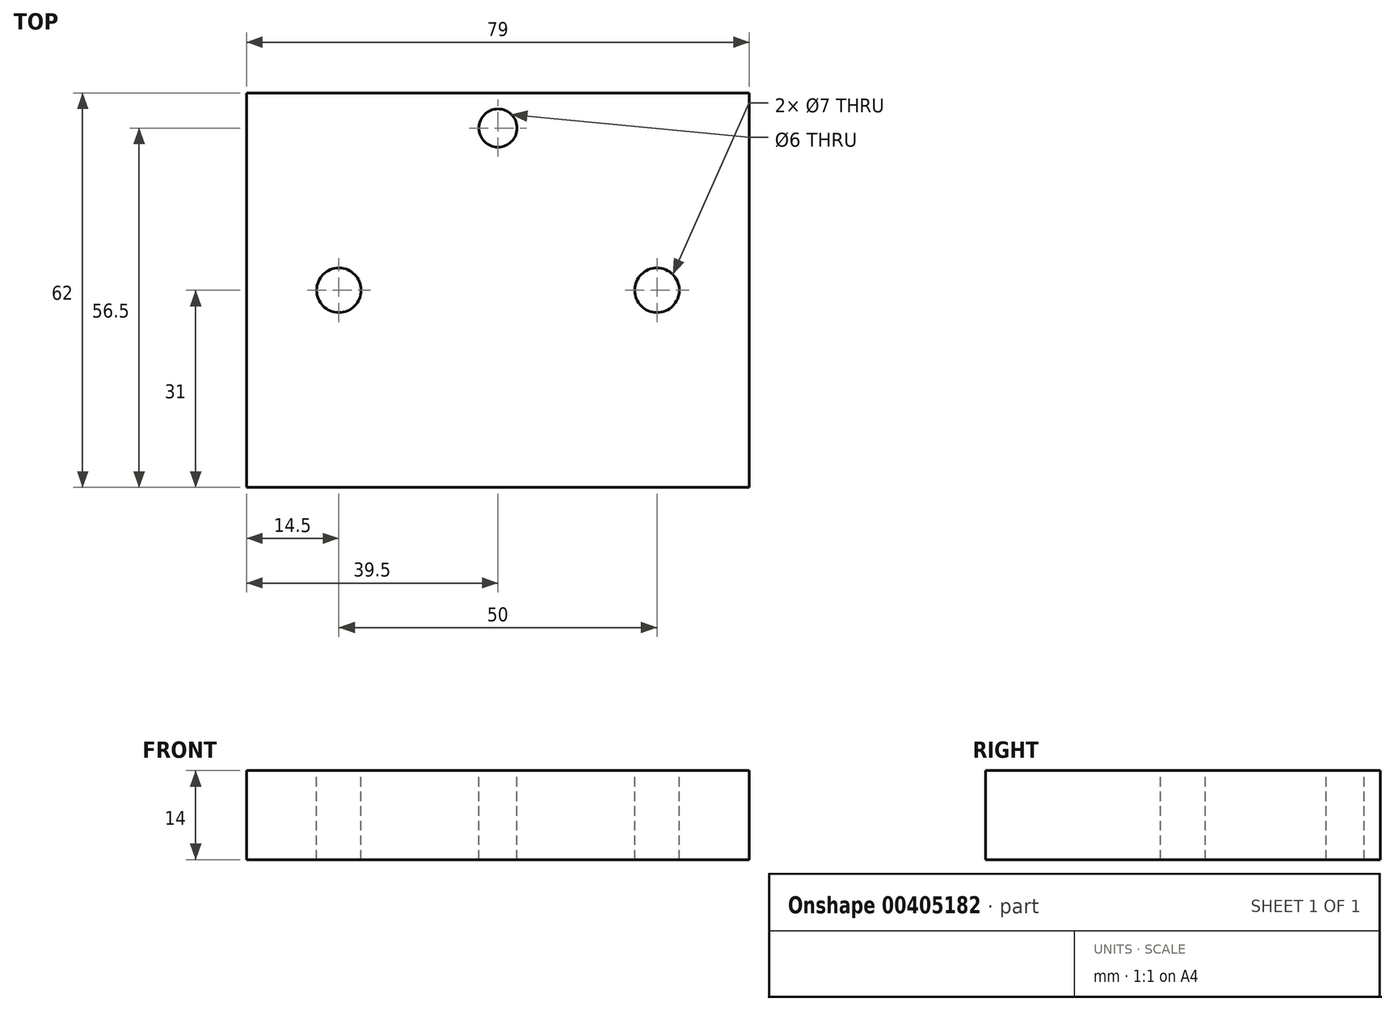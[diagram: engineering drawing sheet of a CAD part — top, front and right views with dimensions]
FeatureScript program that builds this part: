
annotation { "Feature Type Name" : "Feature", "Feature Type Description" : "" }
export const myFeature = defineFeature(function(context is Context, id is Id, definition is map)
    precondition{}
    {
        {
            var Q0;
            Q0=qCreatedBy(makeId("Top.planeOp"),FACE);
            var sketch = newSketch(context, id + "F0", { "sketchPlane" : qUnion([Q0])});
            skLineSegment(sketch, "E0.bottom", {"start": v(0, 0) * mm, "end": v(79, 0) * mm});
            skLineSegment(sketch, "E0.top", {"start": v(0, 62) * mm, "end": v(79, 62) * mm});
            skLineSegment(sketch, "E0.left", {"start": v(0, 0) * mm, "end": v(0, 62) * mm});
            skLineSegment(sketch, "E0.right", {"start": v(79, 0) * mm, "end": v(79, 62) * mm});
            skSolve(sketch);
        }
        {
            var Q0;
            Q0=makeQuery(id+"F0.imprint","IMPRINT",FACE,{"disambiguationData":[TD([[makeQuery(id+"F0.imprint","IMPRINT",EDGE,{"derivedFrom":sQuery(id+"F0.wireOp",EDGE,"E0.bottom")}),1.0]])]});
            var sketch = newSketch(context, id + "F1", { "sketchPlane" : qUnion([Q0])});
            skCircle(sketch, "E1", {"center": v(39.5, 56.5) * mm, "radius": 3 * mm});
            skCircle(sketch, "E2", {"center": v(64.5, 31) * mm, "radius": 3.5 * mm});
            skCircle(sketch, "E3", {"center": v(14.5, 31) * mm, "radius": 3.5 * mm});
            skSolve(sketch);
        }
        {
            var Q0;
            Q0 = qSketchRegion(id + "F0", true);
            extrude(context, id + "F2", {"entities" : qUnion([Q0]), "oppositeDirection" : true, "depth" : 14 * mm});
        }
        {
            var Q0;
            Q0=makeQuery(id+"F1.imprint","IMPRINT",FACE,{"disambiguationData":[TD([[makeQuery(id+"F1.imprint","IMPRINT",EDGE,{"derivedFrom":sQuery(id+"F1.wireOp",EDGE,"E3")}),1.0]])]});
            var Q1;
            Q1=makeQuery(id+"F1.imprint","IMPRINT",FACE,{"disambiguationData":[TD([[makeQuery(id+"F1.imprint","IMPRINT",EDGE,{"derivedFrom":sQuery(id+"F1.wireOp",EDGE,"E1")}),1.0]])]});
            var Q2;
            Q2=makeQuery(id+"F1.imprint","IMPRINT",FACE,{"disambiguationData":[TD([[makeQuery(id+"F1.imprint","IMPRINT",EDGE,{"derivedFrom":sQuery(id+"F1.wireOp",EDGE,"E2")}),1.0]])]});
            extrude(context, id + "F3", {"entities" : qUnion([Q0, Q1, Q2]), "operationType" : NewBodyOperationType.REMOVE, "endBound" : BoundingType.THROUGH_ALL, "oppositeDirection" : true, "depth" : 25 * mm});
        }
    });
